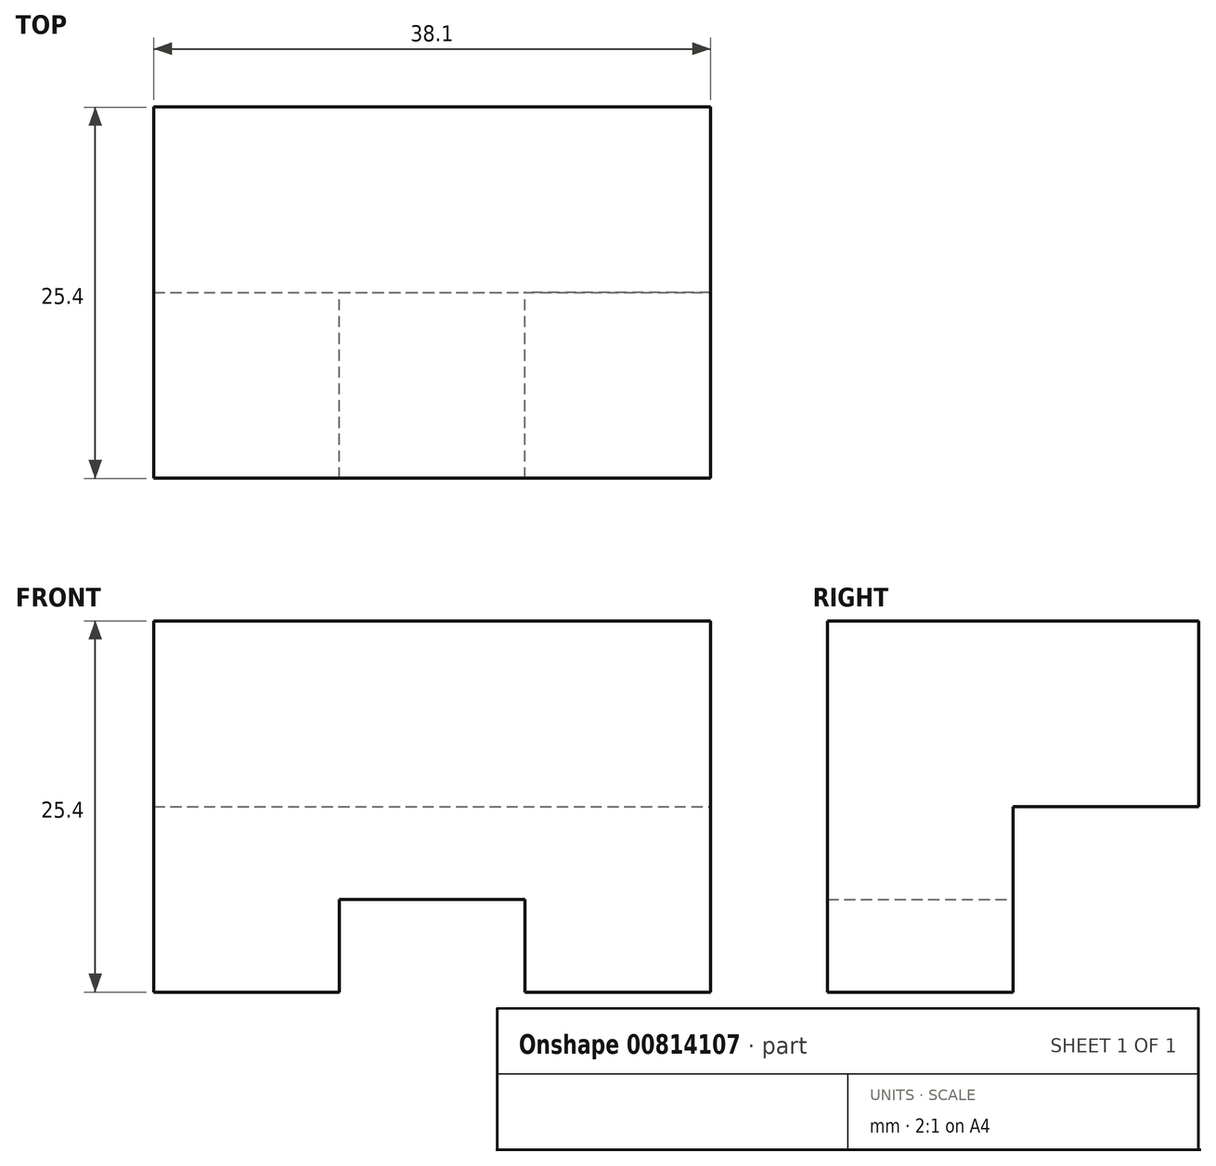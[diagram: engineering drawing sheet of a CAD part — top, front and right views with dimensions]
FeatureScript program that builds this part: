
annotation { "Feature Type Name" : "Feature", "Feature Type Description" : "" }
export const myFeature = defineFeature(function(context is Context, id is Id, definition is map)
    precondition{}
    {
        {
            var Q0;
            Q0=qCreatedBy(makeId("Top.planeOp"),FACE);
            var sketch = newSketch(context, id + "F0", { "sketchPlane" : qUnion([Q0])});
            skLineSegment(sketch, "E0", {"start": v(-38.1, 15.01) * mm, "end": v(-38.1, -10.39) * mm});
            skLineSegment(sketch, "E1", {"start": v(-38.1, 15.01) * mm, "end": v(0, 15.01) * mm});
            skLineSegment(sketch, "E2", {"start": v(0, 15.01) * mm, "end": v(0, -10.39) * mm});
            skLineSegment(sketch, "E3", {"start": v(-38.1, -10.39) * mm, "end": v(0, -10.39) * mm});
            skSolve(sketch);
        }
        {
            var Q0;
            Q0 = qSketchRegion(id + "F0", true);
            extrude(context, id + "F1", {"entities" : qUnion([Q0]), "depth" : 31.75 * mm, "offsetDistance" : 25.4 * mm});
        }
        {
            var Q0;
            Q0=makeQuery(id+"F1.opExtrude","SWEPT_FACE",FACE,{"disambiguationData":[OSD([sQuery(id+"F0.wireOp",EDGE,"E3")])]});
            var sketch = newSketch(context, id + "F2", { "sketchPlane" : qUnion([Q0])});
            skLineSegment(sketch, "E4", {"start": v(-38.1, 0) * mm, "end": v(-38.1, 12.7) * mm});
            skLineSegment(sketch, "E5", {"start": v(-38.1, 12.7) * mm, "end": v(-19.05, 12.7) * mm});
            skLineSegment(sketch, "E6", {"start": v(-19.05, 12.7) * mm, "end": v(-19.05, 25.4) * mm});
            skLineSegment(sketch, "E7", {"start": v(-38.1, 25.4) * mm, "end": v(0, 25.4) * mm});
            skSolve(sketch);
        }
        {
            var Q0;
            {var subQ0=sQuery(id+"F0.wireOp",EDGE,"E3");var subQ1=makeQuery(id+"F1.opExtrude","CAP_EDGE",EDGE,{"disambiguationData":[OSD([subQ0])],"isStart":false});Q0=makeQuery(id+"F2.imprint","IMPRINT",FACE,{"disambiguationData":[TD([[makeQuery(id+"F2.imprint","IMPRINT",EDGE,{"derivedFrom":subQ1}),-1.0]])]});}
            var Q1;
            {var subQ0=sQuery(id+"F2.wireOp",EDGE,"E5");Q1=makeQuery(id+"F2.imprint","IMPRINT",FACE,{"disambiguationData":[TD([[makeQuery(id+"F2.imprint","IMPRINT",EDGE,{"derivedFrom":subQ0}),1.0]])]});}
            extrude(context, id + "F3", {"entities" : qUnion([Q0, Q1]), "operationType" : NewBodyOperationType.REMOVE, "oppositeDirection" : true, "depth" : 25.4 * mm, "offsetDistance" : 25.4 * mm});
        }
        {
            var Q0;
            Q0=makeQuery(id+"F1.opExtrude","SWEPT_FACE",FACE,{"disambiguationData":[OSD([sQuery(id+"F0.wireOp",EDGE,"E1")])]});
            var sketch = newSketch(context, id + "F4", { "sketchPlane" : qUnion([Q0])});
            skLineSegment(sketch, "E8", {"start": v(38.1, 12.7) * mm, "end": v(38.1, 18.98) * mm});
            skLineSegment(sketch, "E9", {"start": v(38.1, 0) * mm, "end": v(25.4, 0) * mm});
            skLineSegment(sketch, "E10", {"start": v(0, 0) * mm, "end": v(12.7, 0) * mm});
            skLineSegment(sketch, "E11", {"start": v(25.4, 0) * mm, "end": v(25.4, 6.35) * mm});
            skLineSegment(sketch, "E12", {"start": v(25.4, 6.35) * mm, "end": v(12.7, 6.35) * mm});
            skLineSegment(sketch, "E13", {"start": v(12.7, 0) * mm, "end": v(12.7, 6.35) * mm});
            skSolve(sketch);
        }
        {
            var Q0;
            {var subQ0=sQuery(id+"F4.wireOp",EDGE,"E11");Q0=makeQuery(id+"F4.imprint","IMPRINT",FACE,{"disambiguationData":[TD([[makeQuery(id+"F4.imprint","IMPRINT",EDGE,{"derivedFrom":subQ0}),1.0]])]});}
            extrude(context, id + "F5", {"entities" : qUnion([Q0]), "operationType" : NewBodyOperationType.REMOVE, "oppositeDirection" : true, "depth" : 25.4 * mm, "offsetDistance" : 25.4 * mm});
        }
        {
            var Q0;
            Q0=makeQuery(id+"F3.boolean.opBoolean","COPY",FACE,{"derivedFrom":makeQuery(id+"F3.opExtrude","SWEPT_FACE",FACE,{"disambiguationData":[OSD([sQuery(id+"F2.wireOp",EDGE,"E6")])]})});
            extrude(context, id + "F6", {"entities" : qUnion([Q0]), "operationType" : NewBodyOperationType.ADD, "depth" : 19.05 * mm, "offsetDistance" : 25.4 * mm});
        }
        {
            var Q0;
            {var subQ0=sQuery(id+"F0.wireOp",EDGE,"E0");var subQ1=sQuery(id+"F0.wireOp",EDGE,"E3");var subQ2=sQuery(id+"F0.wireOp",EDGE,"E1");Q0=makeQuery(id+"F5.boolean.opBoolean","SPLIT",FACE,{"disambiguationData":[TD([makeQuery(id+"F1.opExtrude","SWEPT_FACE",FACE,{"disambiguationData":[OSD([subQ0])]})])],"derivedFrom":makeQuery(id+"F1.opExtrude","CAP_FACE",FACE,{"disambiguationData":[OSD([subQ0,subQ2,sQuery(id+"F0.wireOp",EDGE,"E2"),subQ1])],"isStart":true})});}
            var sketch = newSketch(context, id + "F7", { "sketchPlane" : qUnion([Q0])});
            skLineSegment(sketch, "E14", {"start": v(-38.1, -15.01) * mm, "end": v(-38.1, -2.31) * mm});
            skLineSegment(sketch, "E15", {"start": v(-38.1, -2.31) * mm, "end": v(-25.4, -2.31) * mm});
            skSolve(sketch);
        }
        {
            var Q0;
            Q0 = qSketchRegion(id + "F7", true);
            var Q1;
            Q1=makeQuery(id+"F7.imprint","IMPRINT",FACE,{"disambiguationData":[TD([[makeQuery(id+"F7.imprint","IMPRINT",EDGE,{"derivedFrom":sQuery(id+"F7.wireOp",EDGE,"E14")}),-1.0]])]});
            extrude(context, id + "F8", {"entities" : qUnion([Q0, Q1]), "operationType" : NewBodyOperationType.REMOVE, "oppositeDirection" : true, "depth" : 25.4 * mm, "offsetDistance" : 25.4 * mm});
        }
        {
            var Q0;
            {var subQ0=sQuery(id+"F0.wireOp",EDGE,"E1");var subQ1=sQuery(id+"F0.wireOp",EDGE,"E2");var subQ2=sQuery(id+"F0.wireOp",EDGE,"E3");Q0=makeQuery(id+"F5.boolean.opBoolean","SPLIT",FACE,{"disambiguationData":[TD([makeQuery(id+"F1.opExtrude","SWEPT_FACE",FACE,{"disambiguationData":[OSD([subQ1])]})])],"derivedFrom":makeQuery(id+"F1.opExtrude","CAP_FACE",FACE,{"disambiguationData":[OSD([sQuery(id+"F0.wireOp",EDGE,"E0"),subQ0,subQ1,subQ2])],"isStart":true})});}
            var sketch = newSketch(context, id + "F9", { "sketchPlane" : qUnion([Q0])});
            skLineSegment(sketch, "E16", {"start": v(0, -15.01) * mm, "end": v(0, -2.31) * mm});
            skLineSegment(sketch, "E17", {"start": v(0, -2.31) * mm, "end": v(-12.7, -2.31) * mm});
            skSolve(sketch);
        }
        {
            var Q0;
            Q0=makeQuery(id+"F9.imprint","IMPRINT",FACE,{"disambiguationData":[TD([[makeQuery(id+"F9.imprint","IMPRINT",EDGE,{"derivedFrom":sQuery(id+"F9.wireOp",EDGE,"E16")}),1.0]])]});
            extrude(context, id + "F10", {"entities" : qUnion([Q0]), "operationType" : NewBodyOperationType.REMOVE, "oppositeDirection" : true, "depth" : 25.4 * mm, "offsetDistance" : 25.4 * mm});
        }
        {
            var Q0;
            Q0=makeQuery(id+"F5.boolean.opBoolean","COPY",FACE,{"derivedFrom":makeQuery(id+"F5.opExtrude","SWEPT_FACE",FACE,{"disambiguationData":[OSD([sQuery(id+"F4.wireOp",EDGE,"E12")])]})});
            var sketch = newSketch(context, id + "F11", { "sketchPlane" : qUnion([Q0])});
            skLineSegment(sketch, "E18", {"start": v(-25.4, -2.31) * mm, "end": v(-12.7, -2.31) * mm});
            skSolve(sketch);
        }
        {
            var Q0;
            Q0=makeQuery(id+"F11.imprint","IMPRINT",FACE,{"disambiguationData":[TD([[makeQuery(id+"F11.imprint","IMPRINT",EDGE,{"derivedFrom":sQuery(id+"F11.wireOp",EDGE,"E18")}),-1.0]])]});
            extrude(context, id + "F12", {"entities" : qUnion([Q0]), "operationType" : NewBodyOperationType.REMOVE, "oppositeDirection" : true, "depth" : 25.4 * mm, "offsetDistance" : 25.4 * mm});
        }
        {
            var Q0;
            Q0=makeQuery(id+"F12.boolean.opBoolean","MERGE",FACE,{"derivedFrom":[makeQuery(id+"F8.boolean.opBoolean","COPY",FACE,{"derivedFrom":makeQuery(id+"F8.opExtrude","SWEPT_FACE",FACE,{"disambiguationData":[OSD([sQuery(id+"F7.wireOp",EDGE,"E15")])]})}),makeQuery(id+"F10.boolean.opBoolean","COPY",FACE,{"derivedFrom":makeQuery(id+"F10.opExtrude","SWEPT_FACE",FACE,{"disambiguationData":[OSD([sQuery(id+"F9.wireOp",EDGE,"E17")])]})}),makeQuery(id+"F12.opExtrude","SWEPT_FACE",FACE,{"disambiguationData":[OSD([sQuery(id+"F11.wireOp",EDGE,"E18")])]})]});
            var sketch = newSketch(context, id + "F13", { "sketchPlane" : qUnion([Q0])});
            skLineSegment(sketch, "E19", {"start": v(0, 25.4) * mm, "end": v(0, 12.7) * mm});
            skLineSegment(sketch, "E20", {"start": v(-34.67, 22.23) * mm, "end": v(-28.21, 25.4) * mm});
            skLineSegment(sketch, "E21", {"start": v(38.1, 25.4) * mm, "end": v(38.1, 12.7) * mm});
            skLineSegment(sketch, "E22", {"start": v(38.1, 12.7) * mm, "end": v(0, 12.7) * mm});
            skSolve(sketch);
        }
        {
            var Q0;
            Q0 = qSketchRegion(id + "F13", true);
            var Q1;
            Q1=makeQuery(id+"F13.imprint","IMPRINT",FACE,{"disambiguationData":[TD([[makeQuery(id+"F13.imprint","IMPRINT",EDGE,{"derivedFrom":sQuery(id+"F13.wireOp",EDGE,"E19")}),1.0]])]});
            extrude(context, id + "F14", {"entities" : qUnion([Q0, Q1]), "operationType" : NewBodyOperationType.ADD, "depth" : 12.7 * mm, "offsetDistance" : 25.4 * mm});
        }
    });
